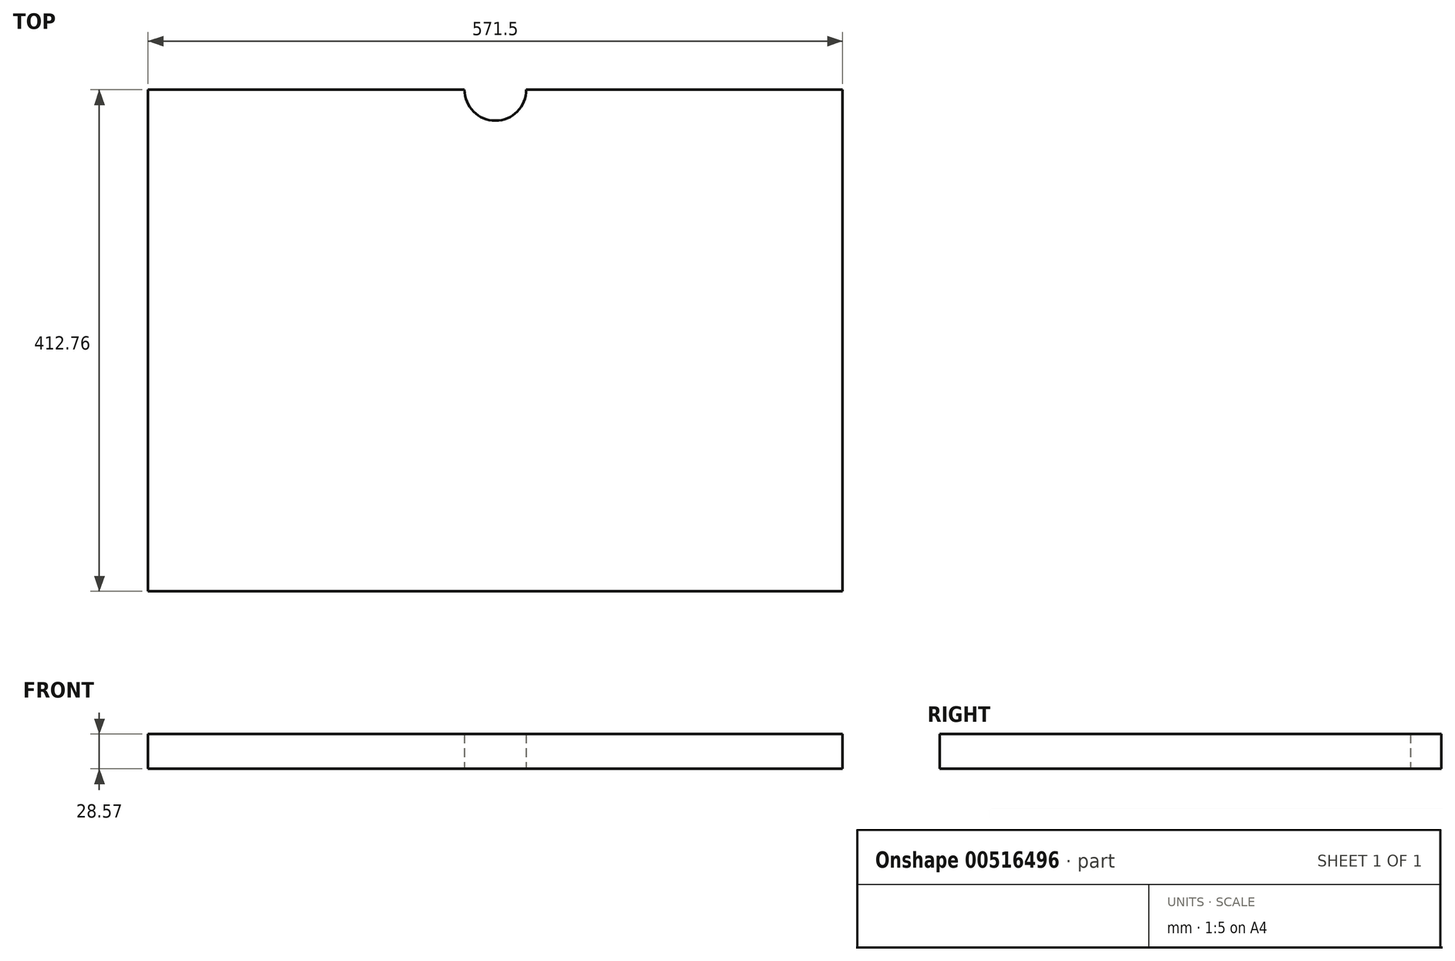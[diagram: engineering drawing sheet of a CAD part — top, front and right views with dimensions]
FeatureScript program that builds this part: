
annotation { "Feature Type Name" : "Feature", "Feature Type Description" : "" }
export const myFeature = defineFeature(function(context is Context, id is Id, definition is map)
    precondition{}
    {
        {
            var Q0;
            Q0=qCreatedBy(makeId("Top.planeOp"),FACE);
            var sketch = newSketch(context, id + "F0", { "sketchPlane" : qUnion([Q0])});
            skLineSegment(sketch, "E0.bottom", {"start": v(285.75, -206.38) * mm, "end": v(-285.75, -206.38) * mm});
            skLineSegment(sketch, "E0.top", {"start": v(285.75, 206.38) * mm, "end": v(-285.75, 206.38) * mm});
            skLineSegment(sketch, "E0.left", {"start": v(285.75, -206.38) * mm, "end": v(285.75, 206.38) * mm});
            skLineSegment(sketch, "E0.right", {"start": v(-285.75, -206.38) * mm, "end": v(-285.75, 206.38) * mm});
            skPoint(sketch, "E0.middle", {"position": v(0, 0) * mm});
            skCircle(sketch, "E1", {"center": v(0, 206.38) * mm, "radius": 25.4 * mm});
            skSolve(sketch);
        }
        {
            var Q0;
            Q0=makeQuery(id+"F0.imprint","IMPRINT",FACE,{"disambiguationData":[TD([[makeQuery(id+"F0.imprint","IMPRINT",EDGE,{"derivedFrom":sQuery(id+"F0.wireOp",EDGE,"E0.bottom")}),-1.0]])]});
            extrude(context, id + "F1", {"entities" : qUnion([Q0]), "depth" : 19.05 * mm, "offsetDistance" : 25.4 * mm});
        }
        {
            var Q0;
            Q0=makeQuery(id+"F1.opExtrude","CAP_FACE",FACE,{"disambiguationData":[OSD([sQuery(id+"F0.wireOp",EDGE,"E0.bottom"),sQuery(id+"F0.wireOp",EDGE,"E0.top"),sQuery(id+"F0.wireOp",EDGE,"E0.left"),sQuery(id+"F0.wireOp",EDGE,"E0.right"),sQuery(id+"F0.wireOp",EDGE,"E1")])],"isStart":false});
            extrude(context, id + "F2", {"entities" : qUnion([Q0]), "operationType" : NewBodyOperationType.ADD, "depth" : 9.52 * mm, "offsetDistance" : 25.4 * mm});
        }
    });
